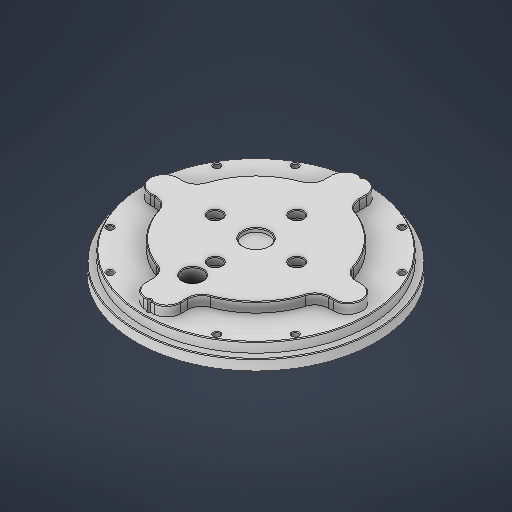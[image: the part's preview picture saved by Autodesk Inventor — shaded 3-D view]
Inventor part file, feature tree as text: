
AUTODESK INVENTOR PART (.ipt)
format: ipt  version: 2025 (Build 290162000, 162)  size: 556,032 bytes
history: native  units: in
note: dims shown in document units (in); Inventor stores cm internally (conversion verified against a paired STEP export)
features: sketch x13, extrude x8, hole x4, chamfer x4
ambient origin geometry x8: Origin, YZ Plane, XZ Plane, XY Plane, X Axis, Y Axis, Z Axis, Center Point
bodies: Solid1 (feature_tree)
feature tree (29):
  sketch  "Sketch1"  dims[d3=4.3307in d24=6.6929in]
  extrude  "Extrusion1"  Depth=6.6929in
  extrude  "Extrusion2"  Depth=5.9843in
  extrude  "Extrusion3"  Depth=4.3307in
  sketch  "Sketch2"  dims[d27=0.9843in d28=4.3307in]
  extrude  "Extrusion4"  Depth=0.3937in
  hole  "Hole1"  [1 undecoded]
  hole  "Hole2"  [1 undecoded]
  sketch  "Sketch4"  dims[d38=0.2953in d39=0.0in d40=2.2835in]
  extrude  "Extrusion5"  Depth=2.2835in
  extrude  "Extrusion6"  Depth=0.1969in
  hole  "Hole3"  [1 undecoded]
  chamfer  "Chamfer1"  Distance=0.7874in Angle=360.0deg
  chamfer  "Chamfer2"  Distance=3.1496in
  hole  "Hole5"  [1 undecoded]
  extrude  "Extrusion9"  Depth=0.3937in
  chamfer  "Chamfer3"  Distance=0.0591in
  extrude  "Extrusion10"  Depth=0.3937in TaperAngle=0.0deg
  chamfer  "Chamfer4"  Distance=0.1969in
  sketch  "Sketch Circular Pattern1"  dims[d25=6.2992in d26=5.9843in]
  sketch  "Sketch3"  dims[d31=0.3937in d32=0.3937in]
  sketch  "Sketch Circular Pattern2"  dims[d29=0.7874in d30=0.3937in]
  sketch  "Sketch5"  dims[d41=0.3543in d42=0.1969in]
  sketch  "Sketch Circular Pattern3"  dims[d34=0.8465in d35=0.0in d36=0.5709in d37=0.0in]
  sketch  "Sketch7"  dims[d56=5.9843in]
  sketch  "Sketch Circular Pattern5"  dims[d43=1.5748in d45=360.0deg d47=0.1969in d48=0.0in]
  sketch  "Sketch9"  dims[d57=0.1378in d58=0.7874in d60=360.0deg]
  sketch  "Sketch Circular Pattern6"  dims[d49=0.2165in d50=0.7874in d51=0.1575in d52=0.0787in d53=90.0deg d54=0.315in d55=0.8108in]
  sketch  "Sketch10"  dims[d62=0.0968in d63=1.0487in d64=0.1575in d65=0.0787in d66=90.0deg d67=0.4646in d68=0.8108in d69=3.1496in d70=0.1969in d71=0.7874in d72=0.0591in d73=0.0in d74=0.4724in d75=0.0in d76=0.1969in d77=4.7244in d79=360.0deg d81=0.1628in d82=0.3937in d83=0.1575in d84=0.0787in d85=90.0deg d86=0.3937in d87=0.8108in d88=0.0197in d89=0.0787in d90=45.0deg d91=0.0197in d92=0.0787in d93=45.0deg d107=3.7402in d108=0.1969in d109=6.2992in d111=360.0deg d113=0.1969in d114=0.7874in d115=0.748in d116=0.3543in d117=90.0deg d118=0.7874in d119=0.8108in d139=0.7185in d140=3.1496in d141=0.7185in d142=3.1496in d144=360.0deg d146=0.0984in d147=0.0in d148=0.0197in d149=0.0787in d150=45.0deg d151=0.5512in d152=1.7717in d153=0.0in d154=0.0in d155=0.0197in d156=0.0787in d157=45.0deg d158=0.5512in d159=1.7717in d137=0.0197in d138=0.0344in]
note: 4 required parameter values undecoded (feature->parameter linkage not recoverable at this tier; creation-order binding heuristic only, values carry confidence <= 0.55)
